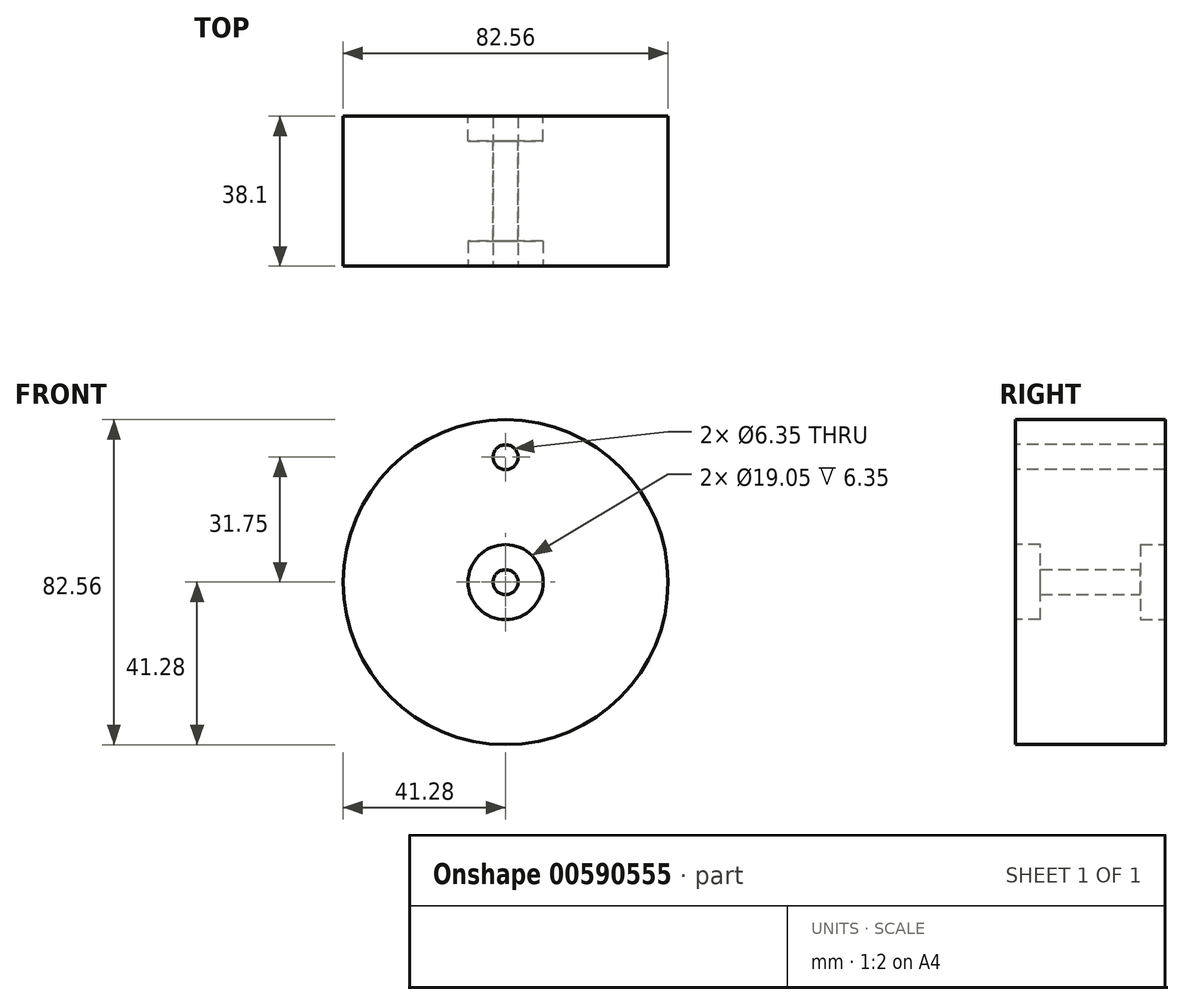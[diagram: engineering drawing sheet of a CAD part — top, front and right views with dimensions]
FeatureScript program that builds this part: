
annotation { "Feature Type Name" : "Feature", "Feature Type Description" : "" }
export const myFeature = defineFeature(function(context is Context, id is Id, definition is map)
    precondition{}
    {
        {
            var Q0;
            Q0=qCreatedBy(makeId("Front.planeOp"),FACE);
            var sketch = newSketch(context, id + "F0", { "sketchPlane" : qUnion([Q0])});
            skCircle(sketch, "E0", {"center": v(0, 0) * mm, "radius": 41.27 * mm});
            skCircle(sketch, "E1", {"center": v(0, 0) * mm, "radius": 3.18 * mm});
            skSolve(sketch);
        }
        {
            var Q0;
            Q0=makeQuery(id+"F0.imprint","IMPRINT",FACE,{"disambiguationData":[TD([[makeQuery(id+"F0.imprint","IMPRINT",EDGE,{"derivedFrom":sQuery(id+"F0.wireOp",EDGE,"E0")}),1.0]])]});
            extrude(context, id + "F1", {"entities" : qUnion([Q0]), "depth" : 38.1 * mm, "offsetDistance" : 25.4 * mm});
        }
        {
            var Q0;
            Q0=makeQuery(id+"F1.opExtrude","CAP_FACE",FACE,{"disambiguationData":[OSD([sQuery(id+"F0.wireOp",EDGE,"E0"),sQuery(id+"F0.wireOp",EDGE,"E1")])],"isStart":false});
            var sketch = newSketch(context, id + "F2", { "sketchPlane" : qUnion([Q0])});
            skCircle(sketch, "E2", {"center": v(0, 31.75) * mm, "radius": 3.18 * mm});
            skSolve(sketch);
        }
        {
            var Q0;
            Q0=makeQuery(id+"F2.imprint","IMPRINT",FACE,{"disambiguationData":[TD([[makeQuery(id+"F2.imprint","IMPRINT",EDGE,{"derivedFrom":sQuery(id+"F2.wireOp",EDGE,"E2")}),1.0]])]});
            extrude(context, id + "F3", {"entities" : qUnion([Q0]), "operationType" : NewBodyOperationType.REMOVE, "endBound" : BoundingType.THROUGH_ALL, "oppositeDirection" : true, "depth" : 25.4 * mm, "offsetDistance" : 25.4 * mm});
        }
        {
            var Q0;
            Q0=makeQuery(id+"F1.opExtrude","CAP_FACE",FACE,{"disambiguationData":[OSD([sQuery(id+"F0.wireOp",EDGE,"E0"),sQuery(id+"F0.wireOp",EDGE,"E1")])],"isStart":false});
            var sketch = newSketch(context, id + "F4", { "sketchPlane" : qUnion([Q0])});
            skCircle(sketch, "E3", {"center": v(0, 0) * mm, "radius": 9.53 * mm});
            skSolve(sketch);
        }
        {
            var Q0;
            Q0=makeQuery(id+"F4.imprint","IMPRINT",FACE,{"disambiguationData":[TD([[makeQuery(id+"F4.imprint","IMPRINT",EDGE,{"derivedFrom":sQuery(id+"F4.wireOp",EDGE,"E3")}),1.0]])]});
            extrude(context, id + "F5", {"entities" : qUnion([Q0]), "operationType" : NewBodyOperationType.REMOVE, "oppositeDirection" : true, "depth" : 6.35 * mm, "offsetDistance" : 25.4 * mm});
        }
        {
            var Q0;
            Q0=makeQuery(id+"F1.opExtrude","CAP_FACE",FACE,{"disambiguationData":[OSD([sQuery(id+"F0.wireOp",EDGE,"E0"),sQuery(id+"F0.wireOp",EDGE,"E1")])],"isStart":true});
            var sketch = newSketch(context, id + "F6", { "sketchPlane" : qUnion([Q0])});
            skCircle(sketch, "E4", {"center": v(0, 0) * mm, "radius": 9.53 * mm});
            skSolve(sketch);
        }
        {
            var Q0;
            Q0=makeQuery(id+"F6.imprint","IMPRINT",FACE,{"disambiguationData":[TD([[makeQuery(id+"F6.imprint","IMPRINT",EDGE,{"derivedFrom":sQuery(id+"F6.wireOp",EDGE,"E4")}),1.0]])]});
            extrude(context, id + "F7", {"entities" : qUnion([Q0]), "operationType" : NewBodyOperationType.REMOVE, "oppositeDirection" : true, "depth" : 6.35 * mm, "offsetDistance" : 25.4 * mm});
        }
    });
